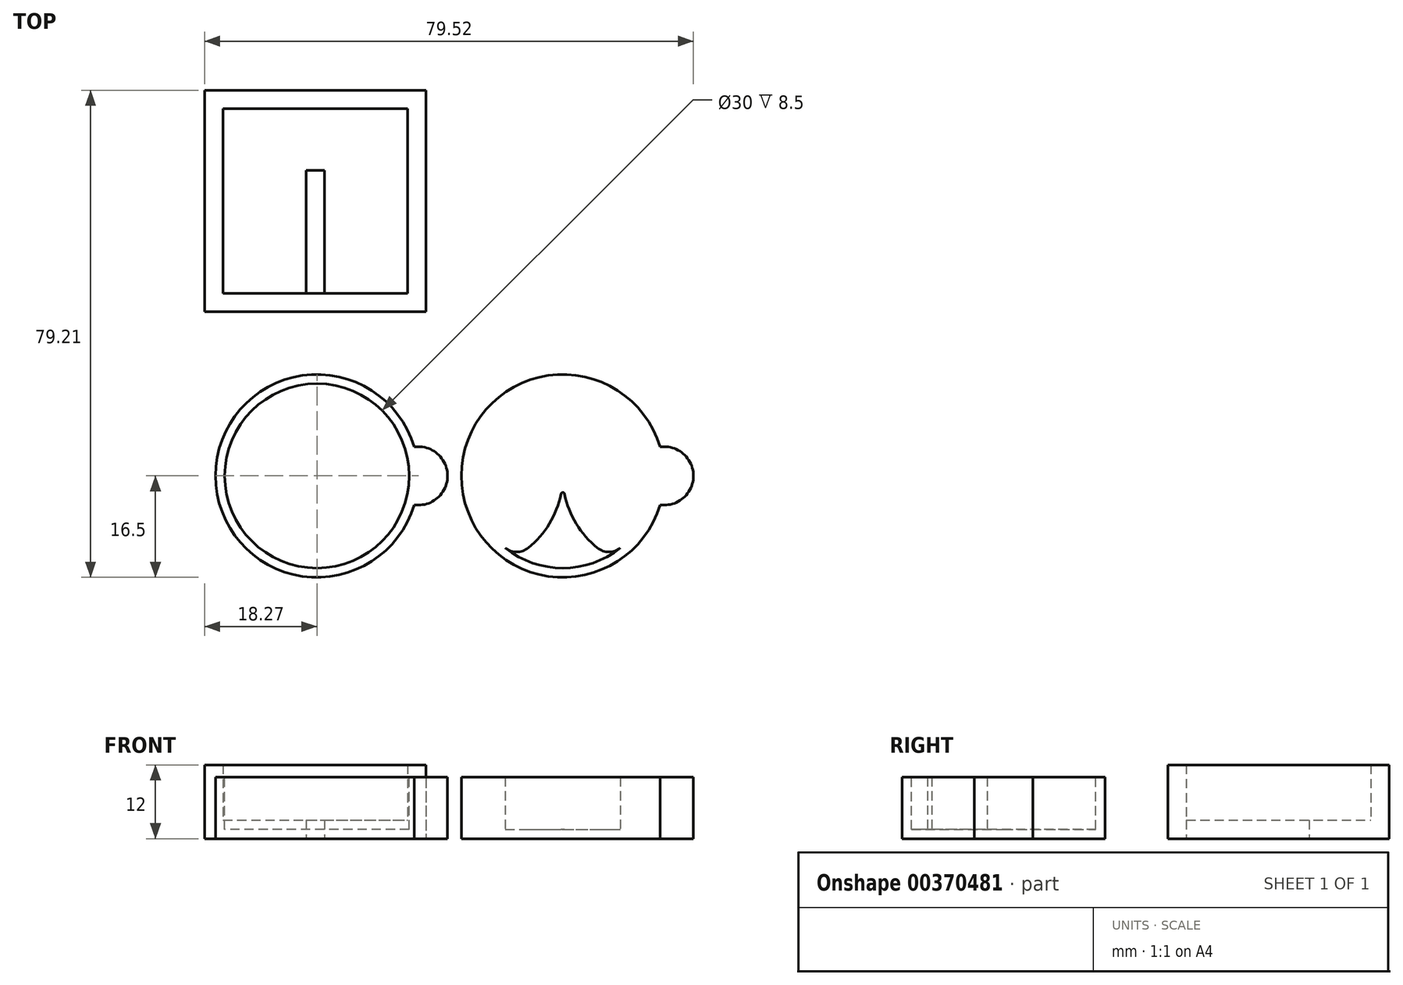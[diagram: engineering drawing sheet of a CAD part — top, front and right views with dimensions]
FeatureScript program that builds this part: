
annotation { "Feature Type Name" : "Feature", "Feature Type Description" : "" }
export const myFeature = defineFeature(function(context is Context, id is Id, definition is map)
    precondition{}
    {
        {
            var Q0;
            Q0=qCreatedBy(makeId("Top.planeOp"),FACE);
            var sketch = newSketch(context, id + "F0", { "sketchPlane" : qUnion([Q0])});
            skCircle(sketch, "E0", {"center": v(0, 0) * mm, "radius": 16.5 * mm});
            skCircle(sketch, "E1", {"center": v(16.5, 0) * mm, "radius": 4.75 * mm});
            skSolve(sketch);
        }
        {
            var Q0;
            Q0 = qSketchRegion(id + "F0", true);
            extrude(context, id + "F1", {"entities" : qUnion([Q0]), "depth" : 10 * mm, "offsetDistance" : 25 * mm});
        }
        {
            var Q0;
            Q0=qCreatedBy(makeId("Top.planeOp"),FACE);
            cPlane(context, id + "F2", {"entities" : qUnion([Q0]), "cplaneType" : CPlaneType.OFFSET, "offset" : 1.5 * mm, "width" : 150 * mm, "height" : 150 * mm});
        }
        {
            var Q0;
            Q0=makeQuery(id+"F1.opExtrude","CAP_FACE",FACE,{"disambiguationData":[OSD([sQuery(id+"F0.wireOp",EDGE,"E0")])],"isStart":false});
            var sketch = newSketch(context, id + "F3", { "sketchPlane" : qUnion([Q0])});
            skCircle(sketch, "E2.0", {"center": v(0, 0) * mm, "radius": 15 * mm});
            skSolve(sketch);
        }
        {
            var Q0;
            Q0=makeQuery(id+"F3.imprint","IMPRINT",FACE,{"disambiguationData":[TD([[makeQuery(id+"F3.imprint","IMPRINT",EDGE,{"derivedFrom":sQuery(id+"F3.wireOp",EDGE,"E2.0")}),1.0]])]});
            var Q1;
            Q1=qCreatedBy(id+"F2.planeOp",FACE);
            extrude(context, id + "F4", {"entities" : qUnion([Q0]), "operationType" : NewBodyOperationType.REMOVE, "endBound" : BoundingType.UP_TO_SURFACE, "oppositeDirection" : true, "endBoundEntityFace" : qUnion([Q1]), "depth" : 8.5 * mm, "offsetDistance" : 25 * mm});
        }
        {
            var Q0;
            Q0=makeQuery(id+"F1.opExtrude","SWEPT_BODY",BODY,{"disambiguationData":[OSD([sQuery(id+"F0.wireOp",EDGE,"E0")])]});
            transform(context, id + "F5", {"entities" : qUnion([Q0]), "transformType" : TransformType.TRANSLATION_3D, "dx" : 40 * mm, "dy" : 0 * mm, "dz" : 0 * mm, "makeCopy" : true});
        }
        {
            var Q0;
            Q0=makeQuery(id+"F5.opPattern","COPY",FACE,{"derivedFrom":makeQuery(id+"F4.boolean.opBoolean","COPY",FACE,{"derivedFrom":makeQuery(id+"F4.opExtrude","CAP_FACE",FACE,{"disambiguationData":[OSD([sQuery(id+"F3.wireOp",EDGE,"E2.0")])],"isStart":false})}),"instanceName":"1"});
            var sketch = newSketch(context, id + "F6", { "sketchPlane" : qUnion([Q0])});
            skArc(sketch, "E3", {"start": v(39.7, 2.94) * mm, "mid": v(37.81, 7.8) * mm, "end": v(34.38, 11.7) * mm});
            skLineSegment(sketch, "E4", {"start": v(40, 31.13) * mm, "end": v(40, -38.73) * mm, "construction": true});
            skPoint(sketch, "E5", {"position": v(40, 0) * mm});
            skLineSegment(sketch, "E6", {"start": v(25, 0) * mm, "end": v(40, 0) * mm, "construction": true});
            skArc(sketch, "E7.0", {"start": v(30.62, 11.7) * mm, "mid": v(26.48, 6.5) * mm, "end": v(25, 0) * mm});
            skPoint(sketch, "E8.center.orphan", {"position": v(32.5, 0) * mm});
            skArc(sketch, "E9", {"start": v(39.7, 2.94) * mm, "mid": v(39.81, 2.77) * mm, "end": v(40, 2.7) * mm});
            skArc(sketch, "E10.MirrorCS", {"start": v(39.7, -2.94) * mm, "mid": v(37.81, -7.8) * mm, "end": v(34.38, -11.7) * mm});
            skArc(sketch, "E11.MirrorCS", {"start": v(39.7, -2.94) * mm, "mid": v(39.81, -2.77) * mm, "end": v(40, -2.7) * mm});
            skArc(sketch, "E12.MirrorCS", {"start": v(30.62, -11.7) * mm, "mid": v(26.48, -6.5) * mm, "end": v(25, 0) * mm});
            skPoint(sketch, "E13.MirrorP", {"position": v(47.5, 0) * mm});
            skArc(sketch, "E14.MirrorCS", {"start": v(40.3, -2.94) * mm, "mid": v(42.19, -7.8) * mm, "end": v(45.62, -11.7) * mm});
            skArc(sketch, "E15.MirrorCS", {"start": v(40.3, 2.94) * mm, "mid": v(42.19, 7.8) * mm, "end": v(45.62, 11.7) * mm});
            skArc(sketch, "E16.MirrorCS", {"start": v(40.3, 2.94) * mm, "mid": v(40.19, 2.77) * mm, "end": v(40, 2.7) * mm});
            skArc(sketch, "E17.MirrorCS", {"start": v(49.38, 11.7) * mm, "mid": v(53.52, 6.5) * mm, "end": v(55, 0) * mm});
            skArc(sketch, "E18.MirrorCS", {"start": v(40.3, -2.94) * mm, "mid": v(40.19, -2.77) * mm, "end": v(40, -2.7) * mm});
            skArc(sketch, "E19.MirrorCS", {"start": v(49.38, -11.7) * mm, "mid": v(53.52, -6.5) * mm, "end": v(55, 0) * mm});
            skArc(sketch, "E20", {"start": v(34.38, 11.7) * mm, "mid": v(32.5, 12.37) * mm, "end": v(30.62, 11.7) * mm});
            skLineSegment(sketch, "E21", {"start": v(32.5, 0) * mm, "end": v(32.5, 22) * mm, "construction": true});
            skArc(sketch, "E22.MirrorC", {"start": v(34.38, -11.7) * mm, "mid": v(32.5, -12.37) * mm, "end": v(30.62, -11.7) * mm});
            skArc(sketch, "E23.MirrorC", {"start": v(45.62, -11.7) * mm, "mid": v(47.5, -12.37) * mm, "end": v(49.38, -11.7) * mm});
            skArc(sketch, "E24.MirrorC", {"start": v(45.62, 11.7) * mm, "mid": v(47.5, 12.37) * mm, "end": v(49.38, 11.7) * mm});
            skSolve(sketch);
        }
        {
            var Q0;
            Q0=makeQuery(id+"F6.imprint","IMPRINT",FACE,{"disambiguationData":[TD([[makeQuery(id+"F6.imprint","IMPRINT",EDGE,{"derivedFrom":sQuery(id+"F6.wireOp",EDGE,"E3")}),-1.0]])]});
            var Q1;
            Q1=makeQuery(id+"F6.imprint","IMPRINT",FACE,{"disambiguationData":[TD([[makeQuery(id+"F6.imprint","IMPRINT",EDGE,{"derivedFrom":sQuery(id+"F6.wireOp",EDGE,"E10.MirrorCS")}),1.0]])]});
            var Q2;
            Q2=makeQuery(id+"F5.opPattern","COPY",FACE,{"derivedFrom":makeQuery(id+"F1.opExtrude","CAP_FACE",FACE,{"disambiguationData":[OSD([sQuery(id+"F0.wireOp",EDGE,"E0"),sQuery(id+"F0.wireOp",EDGE,"E1")])],"isStart":false}),"instanceName":"1"});
            extrude(context, id + "F7", {"entities" : qUnion([Q0, Q1]), "operationType" : NewBodyOperationType.ADD, "endBound" : BoundingType.UP_TO_SURFACE, "depth" : 25 * mm, "endBoundEntityFace" : qUnion([Q2]), "offsetDistance" : 25 * mm});
        }
        {
            var Q0;
            Q0=qCreatedBy(makeId("Top.planeOp"),FACE);
            var sketch = newSketch(context, id + "F8", { "sketchPlane" : qUnion([Q0])});
            skLineSegment(sketch, "E25.bottom", {"start": v(-18.27, 26.71) * mm, "end": v(17.73, 26.71) * mm});
            skLineSegment(sketch, "E25.top", {"start": v(-18.27, 62.71) * mm, "end": v(17.73, 62.71) * mm});
            skLineSegment(sketch, "E25.left", {"start": v(-18.27, 26.71) * mm, "end": v(-18.27, 62.71) * mm});
            skLineSegment(sketch, "E25.right", {"start": v(17.73, 26.71) * mm, "end": v(17.73, 62.71) * mm});
            skLineSegment(sketch, "E26.0", {"start": v(-15.27, 59.71) * mm, "end": v(14.73, 59.71) * mm});
            skLineSegment(sketch, "E26.1", {"start": v(-15.27, 29.71) * mm, "end": v(-15.27, 59.71) * mm});
            skLineSegment(sketch, "E26.2", {"start": v(-15.27, 29.71) * mm, "end": v(14.73, 29.71) * mm});
            skLineSegment(sketch, "E26.3", {"start": v(14.73, 29.71) * mm, "end": v(14.73, 59.71) * mm});
            skLineSegment(sketch, "E27", {"start": v(-0.27, 68.06) * mm, "end": v(-0.27, 25.42) * mm, "construction": true});
            skLineSegment(sketch, "E28.bottom", {"start": v(-1.77, 29.71) * mm, "end": v(1.23, 29.71) * mm});
            skLineSegment(sketch, "E28.top", {"start": v(-1.77, 49.71) * mm, "end": v(1.23, 49.71) * mm});
            skLineSegment(sketch, "E28.left", {"start": v(-1.77, 29.71) * mm, "end": v(-1.77, 49.71) * mm});
            skLineSegment(sketch, "E28.right", {"start": v(1.23, 29.71) * mm, "end": v(1.23, 49.71) * mm});
            skSolve(sketch);
        }
        {
            var Q0;
            Q0=makeQuery(id+"F8.imprint","IMPRINT",FACE,{"disambiguationData":[TD([[makeQuery(id+"F8.imprint","IMPRINT",EDGE,{"derivedFrom":sQuery(id+"F8.wireOp",EDGE,"E25.bottom")}),1.0]])]});
            var Q1;
            Q1=makeQuery(id+"F8.imprint","IMPRINT",FACE,{"disambiguationData":[TD([[makeQuery(id+"F8.imprint","IMPRINT",EDGE,{"derivedFrom":sQuery(id+"F8.wireOp",EDGE,"E28.bottom")}),1.0]])]});
            extrude(context, id + "F9", {"entities" : qUnion([Q0, Q1]), "depth" : 12 * mm, "offsetDistance" : 25 * mm});
        }
        {
            var Q0;
            Q0=makeQuery(id+"F8.imprint","IMPRINT",FACE,{"disambiguationData":[TD([[makeQuery(id+"F8.imprint","IMPRINT",EDGE,{"derivedFrom":sQuery(id+"F8.wireOp",EDGE,"E26.0")}),-1.0]])]});
            extrude(context, id + "F10", {"entities" : qUnion([Q0]), "operationType" : NewBodyOperationType.ADD, "depth" : 3 * mm, "offsetDistance" : 25 * mm});
        }
    });
